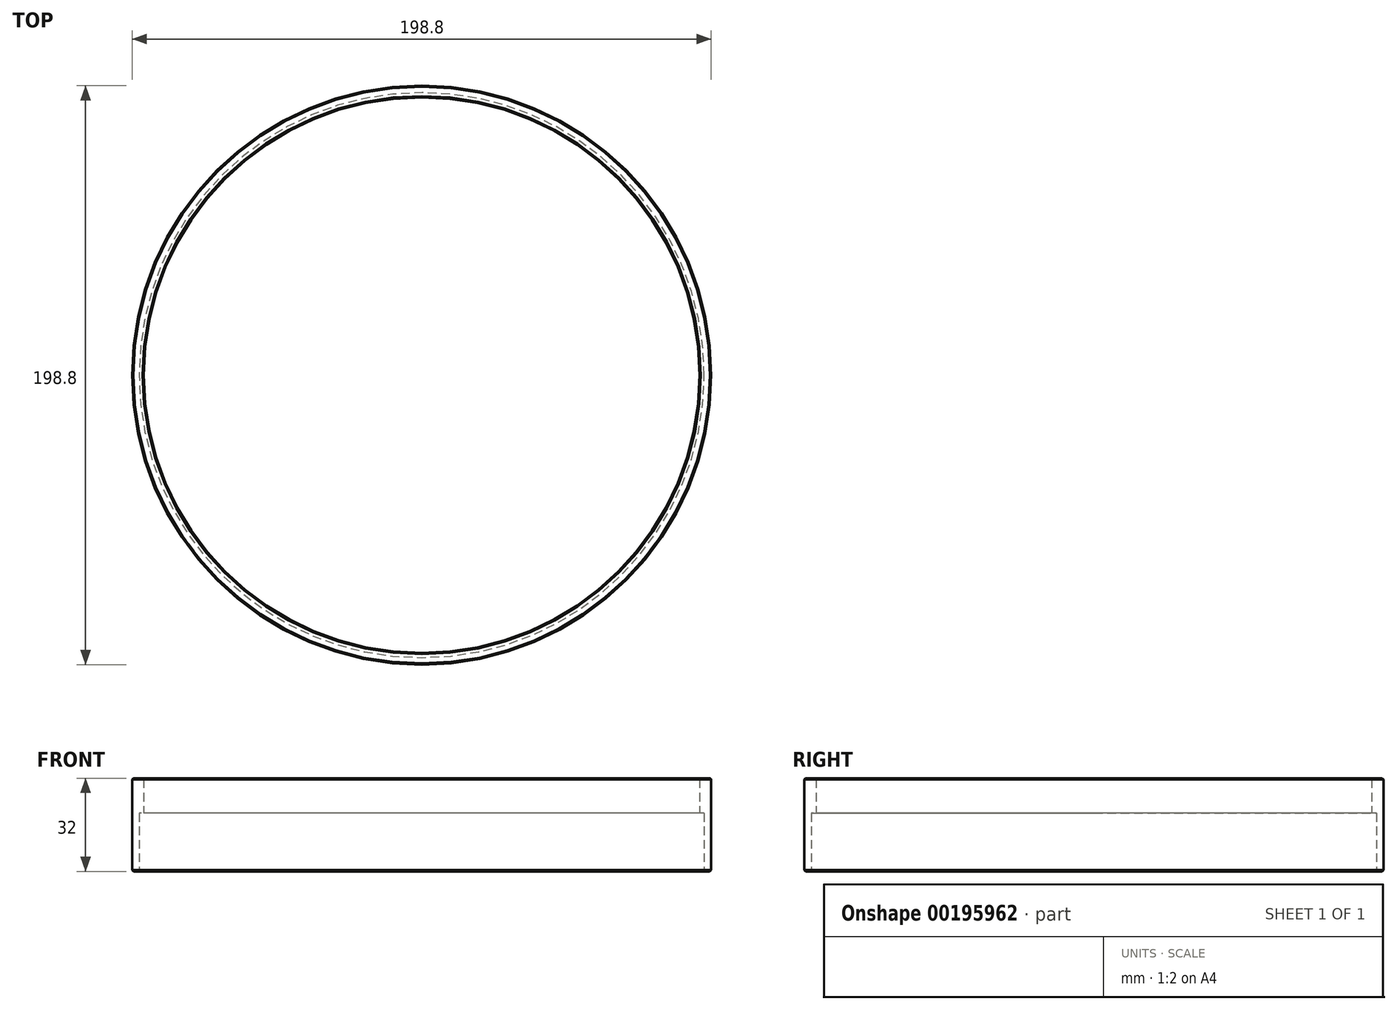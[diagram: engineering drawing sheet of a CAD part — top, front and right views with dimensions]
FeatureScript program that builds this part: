
annotation { "Feature Type Name" : "Feature", "Feature Type Description" : "" }
export const myFeature = defineFeature(function(context is Context, id is Id, definition is map)
    precondition{}
    {
        {
            var Q0;
            Q0=qCreatedBy(makeId("Top.planeOp"),FACE);
            var sketch = newSketch(context, id + "F0", { "sketchPlane" : qUnion([Q0])});
            skCircle(sketch, "E0", {"center": v(0, 0) * mm, "radius": 97 * mm});
            skCircle(sketch, "E1", {"center": v(0, 0) * mm, "radius": 99.4 * mm});
            skSolve(sketch);
        }
        {
            var Q0;
            Q0 = qSketchRegion(id + "F0", true);
            extrude(context, id + "F1", {"entities" : qUnion([Q0]), "depth" : 20 * mm});
        }
        {
            var Q0;
            Q0=makeQuery(id+"F1.opExtrude","CAP_FACE",FACE,{"disambiguationData":[OSD([sQuery(id+"F0.wireOp",EDGE,"E0"),sQuery(id+"F0.wireOp",EDGE,"E1")])],"isStart":false});
            var sketch = newSketch(context, id + "F2", { "sketchPlane" : qUnion([Q0])});
            skCircle(sketch, "E2.0", {"center": v(0, 0) * mm, "radius": 99.4 * mm});
            skCircle(sketch, "E3.0", {"center": v(0, 0) * mm, "radius": 95.4 * mm});
            skSolve(sketch);
        }
        {
            var Q0;
            Q0 = qSketchRegion(id + "F2", true);
            extrude(context, id + "F3", {"entities" : qUnion([Q0]), "operationType" : NewBodyOperationType.ADD, "depth" : 12 * mm});
        }
        {
            var Q0;
            Q0=makeQuery(id+"F3.opExtrude","CAP_EDGE",EDGE,{"disambiguationData":[OSD([sQuery(id+"F2.wireOp",EDGE,"E2.0")])],"isStart":false});
            var Q1;
            Q1=makeQuery(id+"F3.opExtrude","CAP_EDGE",EDGE,{"disambiguationData":[OSD([sQuery(id+"F2.wireOp",EDGE,"E3.0")])],"isStart":false});
            chamfer(context, id + "F4", {"entities" : qUnion([Q0, Q1]), "width" : 0.4 * mm, "tangentPropagation" : true});
        }
        {
            var Q0;
            Q0=makeQuery(id+"F1.opExtrude","CAP_EDGE",EDGE,{"disambiguationData":[OSD([sQuery(id+"F0.wireOp",EDGE,"E1")])],"isStart":true});
            chamfer(context, id + "F5", {"entities" : qUnion([Q0]), "width" : 0.5 * mm, "tangentPropagation" : true});
        }
    });
